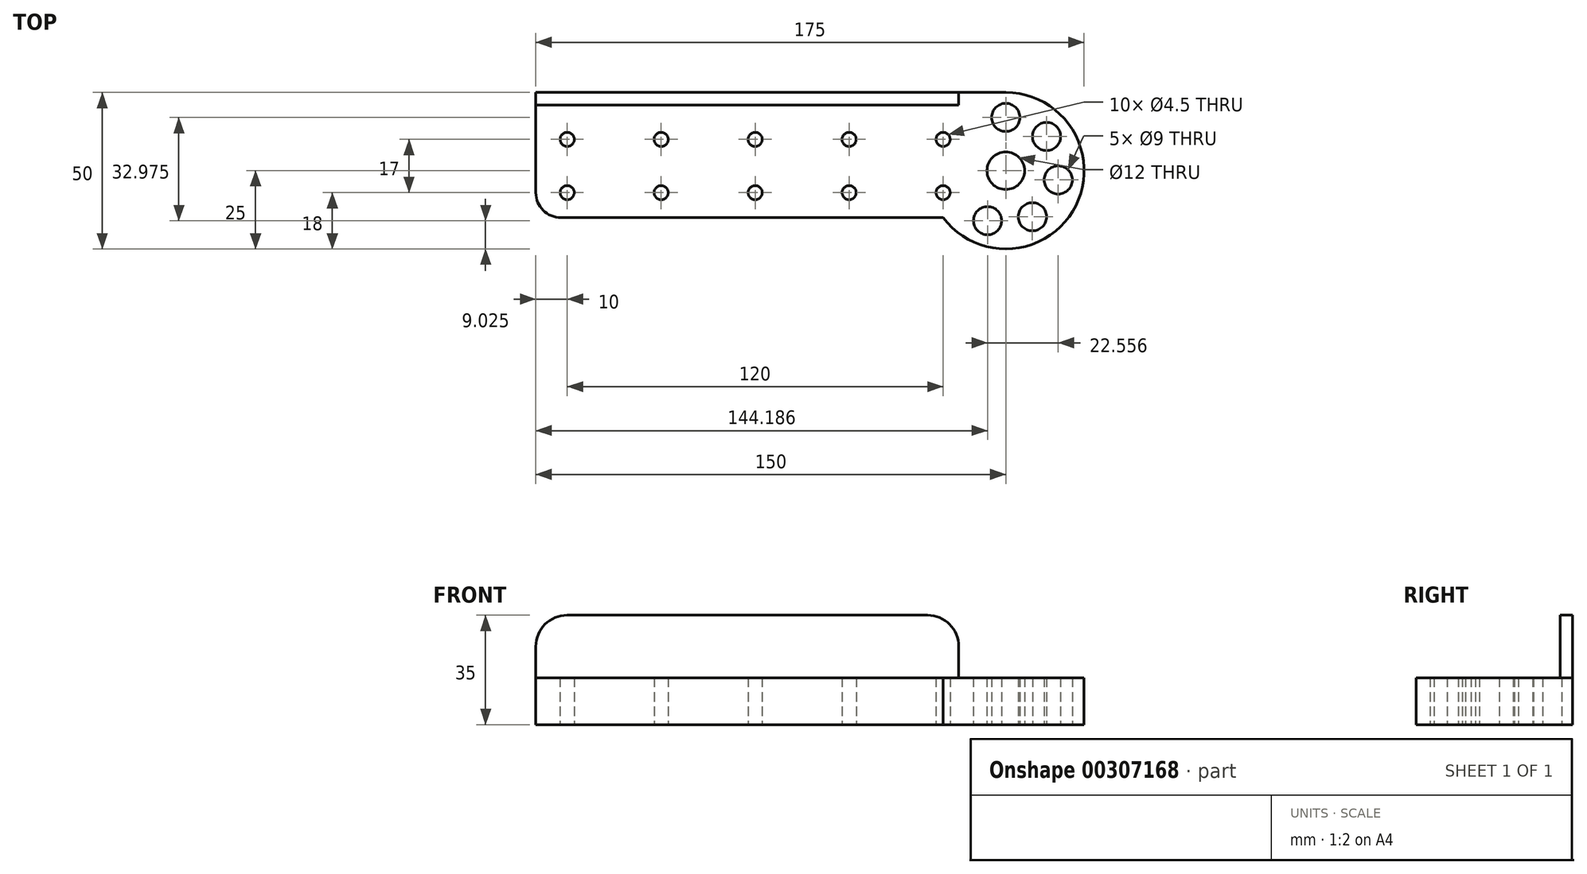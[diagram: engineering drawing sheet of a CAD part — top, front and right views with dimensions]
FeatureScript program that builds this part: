
annotation { "Feature Type Name" : "Feature", "Feature Type Description" : "" }
export const myFeature = defineFeature(function(context is Context, id is Id, definition is map)
    precondition{}
    {
        {
            var Q0;
            Q0=qCreatedBy(makeId("Top.planeOp"),FACE);
            var sketch = newSketch(context, id + "F0", { "sketchPlane" : qUnion([Q0])});
            skLineSegment(sketch, "E0.bottom", {"start": v(8, 0) * mm, "end": v(130, 0) * mm});
            skLineSegment(sketch, "E0.top", {"start": v(0, 40) * mm, "end": v(150, 40) * mm});
            skLineSegment(sketch, "E0.left", {"start": v(0, 8) * mm, "end": v(0, 40) * mm});
            skCircle(sketch, "E1", {"center": v(10, 8) * mm, "radius": 2.25 * mm});
            skCircle(sketch, "E2", {"center": v(10, 25) * mm, "radius": 2.25 * mm});
            skCircle(sketch, "E3.1.0.0", {"center": v(40, 25) * mm, "radius": 2.25 * mm});
            skCircle(sketch, "E3.1.0.1", {"center": v(40, 8) * mm, "radius": 2.25 * mm});
            skCircle(sketch, "E3.2.0.0", {"center": v(70, 25) * mm, "radius": 2.25 * mm});
            skCircle(sketch, "E3.2.0.1", {"center": v(70, 8) * mm, "radius": 2.25 * mm});
            skCircle(sketch, "E3.3.0.0", {"center": v(100, 25) * mm, "radius": 2.25 * mm});
            skCircle(sketch, "E3.3.0.1", {"center": v(100, 8) * mm, "radius": 2.25 * mm});
            skCircle(sketch, "E3.4.0.0", {"center": v(130, 25) * mm, "radius": 2.25 * mm});
            skCircle(sketch, "E3.4.0.1", {"center": v(130, 8) * mm, "radius": 2.25 * mm});
            skLineSegment(sketch, "E3.direction1", {"start": v(10, 25) * mm, "end": v(40, 25) * mm, "construction": true});
            skArc(sketch, "E4", {"start": v(130, 0) * mm, "mid": v(172.36, 3.82) * mm, "end": v(150, 40) * mm});
            skCircle(sketch, "E5", {"center": v(150, 32) * mm, "radius": 4.5 * mm});
            skCircle(sketch, "E6.1.0", {"center": v(163.02, 25.93) * mm, "radius": 4.5 * mm});
            skCircle(sketch, "E6.2.0", {"center": v(166.74, 12.05) * mm, "radius": 4.5 * mm});
            skCircle(sketch, "E6.3.0", {"center": v(158.5, 0.28) * mm, "radius": 4.5 * mm});
            skCircle(sketch, "E6.4.0", {"center": v(144.19, -0.97) * mm, "radius": 4.5 * mm});
            skLineSegment(sketch, "E6.anchor1", {"start": v(150, 15) * mm, "end": v(150, 32) * mm, "construction": true});
            skLineSegment(sketch, "E6.anchor2", {"start": v(150, 15) * mm, "end": v(144.19, -0.97) * mm, "construction": true});
            skCircle(sketch, "E7", {"center": v(150, 15) * mm, "radius": 6 * mm});
            skPoint(sketch, "E8.visualSharp", {"position": v(0, 0) * mm});
            skArc(sketch, "E8.filletArc", {"start": v(0, 8) * mm, "mid": v(2.34, 2.34) * mm, "end": v(8, 0) * mm});
            skSolve(sketch);
        }
        {
            var Q0;
            Q0 = qSketchRegion(id + "F0", true);
            extrude(context, id + "F1", {"entities" : qUnion([Q0]), "depth" : 15 * mm});
        }
        {
            var Q0;
            Q0=makeQuery(id+"F1.opExtrude","CAP_FACE",FACE,{"disambiguationData":[OSD([sQuery(id+"F0.wireOp",EDGE,"E0.bottom"),sQuery(id+"F0.wireOp",EDGE,"E0.top"),sQuery(id+"F0.wireOp",EDGE,"E0.left"),sQuery(id+"F0.wireOp",EDGE,"E1"),sQuery(id+"F0.wireOp",EDGE,"E2"),sQuery(id+"F0.wireOp",EDGE,"E3.1.0.0"),sQuery(id+"F0.wireOp",EDGE,"E3.1.0.1"),sQuery(id+"F0.wireOp",EDGE,"E3.2.0.0"),sQuery(id+"F0.wireOp",EDGE,"E3.2.0.1"),sQuery(id+"F0.wireOp",EDGE,"E3.3.0.0"),sQuery(id+"F0.wireOp",EDGE,"E3.3.0.1"),sQuery(id+"F0.wireOp",EDGE,"E3.4.0.0"),sQuery(id+"F0.wireOp",EDGE,"E3.4.0.1"),sQuery(id+"F0.wireOp",EDGE,"E4"),sQuery(id+"F0.wireOp",EDGE,"E5"),sQuery(id+"F0.wireOp",EDGE,"E6.1.0"),sQuery(id+"F0.wireOp",EDGE,"E6.2.0"),sQuery(id+"F0.wireOp",EDGE,"E6.3.0"),sQuery(id+"F0.wireOp",EDGE,"E6.4.0"),sQuery(id+"F0.wireOp",EDGE,"E7"),sQuery(id+"F0.wireOp",EDGE,"E8.filletArc")])],"isStart":false});
            var sketch = newSketch(context, id + "F2", { "sketchPlane" : qUnion([Q0])});
            skLineSegment(sketch, "E9.bottom", {"start": v(0, 40) * mm, "end": v(135, 40) * mm});
            skLineSegment(sketch, "E9.top", {"start": v(0, 36) * mm, "end": v(135, 36) * mm});
            skLineSegment(sketch, "E9.left", {"start": v(0, 40) * mm, "end": v(0, 36) * mm});
            skLineSegment(sketch, "E9.right", {"start": v(135, 40) * mm, "end": v(135, 36) * mm});
            skSolve(sketch);
        }
        {
            var Q0;
            Q0 = qSketchRegion(id + "F2", true);
            extrude(context, id + "F3", {"entities" : qUnion([Q0]), "operationType" : NewBodyOperationType.ADD, "depth" : 20 * mm});
        }
        {
            var Q0;
            Q0=makeQuery(id+"F3.opExtrude","CAP_EDGE",EDGE,{"disambiguationData":[OSD([sQuery(id+"F2.wireOp",EDGE,"E9.right")])],"isStart":false});
            var Q1;
            Q1=makeQuery(id+"F3.opExtrude","CAP_EDGE",EDGE,{"disambiguationData":[OSD([sQuery(id+"F2.wireOp",EDGE,"E9.left")])],"isStart":false});
            fillet(context, id + "F4", {"entities" : qUnion([Q0, Q1]), "radius" : 10 * mm, "tangentPropagation" : true, "allowEdgeOverflow" : false});
        }
    });
